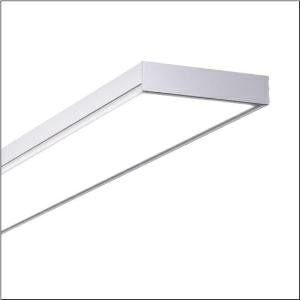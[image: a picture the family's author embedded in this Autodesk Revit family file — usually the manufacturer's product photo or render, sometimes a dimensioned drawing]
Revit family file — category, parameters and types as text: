
# Revit family: apollon_r__31_surface_51mp26wd2341e_c239
name_source: partatom
category: Lighting Fixtures
units: mm (PartAtom-declared; Revit-internal decimal feet)

## family parameters
Cut with Voids When Loaded = No
Host = Face
Light Source = No
Part Type = Normal
Room Calculation Point = No
Round Connector Dimension = Use Diameter
Shared = No

## types (1)
- Apollon® 31 Surface (1 x LED, 4400 lm, 33 W, 3000K)
    Apparent Load = 33 VA
    CIE Flux Codes = 61 87 97 97 100
    Color Rendering = 80
    Color Temperature = 3000K
    Default Elevation = 1800 mm
    Description = Apollon® 31 Surface, office luminaire, primary optical cover: micro prismatic cover, of PMMA, light emission: direct distribution, primary light characteristic: symmetric, installation type: surface-mounted, LED, rated luminous flux: 4.400lm, luminous efficacy: 133lm/W, light colour: 830, colour temperature: 3000K, control gear: ECG DALI, with terminal, 5-pole, mains connection: 220..240V, AC, 50/60Hz, rated input power: 33W, housing, of sheet steel, coil coated, metallic grey (RAL 9006), length: 1.545mm, width: 200mm, height: 44mm, protection rating (complete): IP20, insulation class (complete): insulation class II (safety insulation), certification: CE, impact resistance: IK02, permissible operating ambient temperature: -20..+40°C, standard: EN 60598-2-22, packaging unit: 1 piece
    Height = 44 mm
    Lamp = 1 x LED
    Lamp Light Flux = 4400 lm
    Lamp Power = 33 W
    Lamp count = 1
    Length = 1545 mm
    Luminous efficacy = 133 lm/W
    Manufacturer = Siteco
    ModVariant = No
    Model = 51MP26WD2341E
    Mounting Place = Ceiling
    Mounting Type = Surface mounted
    Number of Poles = 1
    OnlyDefault = Yes
    Power Factor = 1
    Product Name = Apollon® 31 Surface
    Product group = office luminaire | ceiling mounted
    ProductGroupID = 304
    Protection Class = Protection class II
    Protection Degree = IP 20
    RLX_Detail_Level = 1
    RLX_Emergency_Light_Flux = 0 lm
    RLX_Emergency_Type = 0
    RLX_Emergency_Type_DB = No
    RlxData = <blob elided: 24145 chars, md5=d7d2934e>
    Socket = socket
    Standby Power = 0 W
    System Light Flux = 4400 lm
    System Power = 33 W
    Type Comments = Product without accessories
    Type Image = l_1007091.jpg
    URL = http://relux.com
    VarID = ---
    Voltage = 0 V
    Weight = 0.00 kg
    Width = 200 mm  [stored 0.656168 ft]

note: [stored X ft] marks values corroborated as IEEE doubles in the binary element streams (Revit-internal decimal feet)

## geometry (parser evidence)
native form markers: Blend x4, Sweep x10
no freeform markers — native parametric forms only
